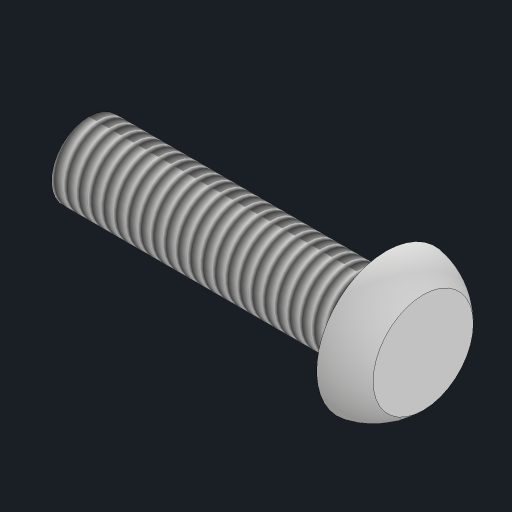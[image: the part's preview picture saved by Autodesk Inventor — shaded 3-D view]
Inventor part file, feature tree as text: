
AUTODESK INVENTOR PART (.ipt)
format: ipt  version: 2023.2 (Build 272271030, 271C)  size: 165,888 bytes
history: native  units: mm
features: revolve x1, thread x1, sketch x1
ambient origin geometry x8: Origin, YZ Plane, XZ Plane, XY Plane, X Axis, Y Axis, Z Axis, Center Point
bodies: Solid1 (feature_tree)
feature tree (3):
  revolve  "Revolution1"  [1 undecoded]
  thread  "Thread1"  [1 undecoded]
  sketch  "Sketch1"  dims[d0=12.0mm d1=1.5mm d2=2.8mm d3=1.5mm d4=0.5mm d5=90.0deg d6=12.0mm d7=0.0mm]
note: 2 required parameter values undecoded (feature->parameter linkage not recoverable at this tier; creation-order binding heuristic only, values carry confidence <= 0.55)